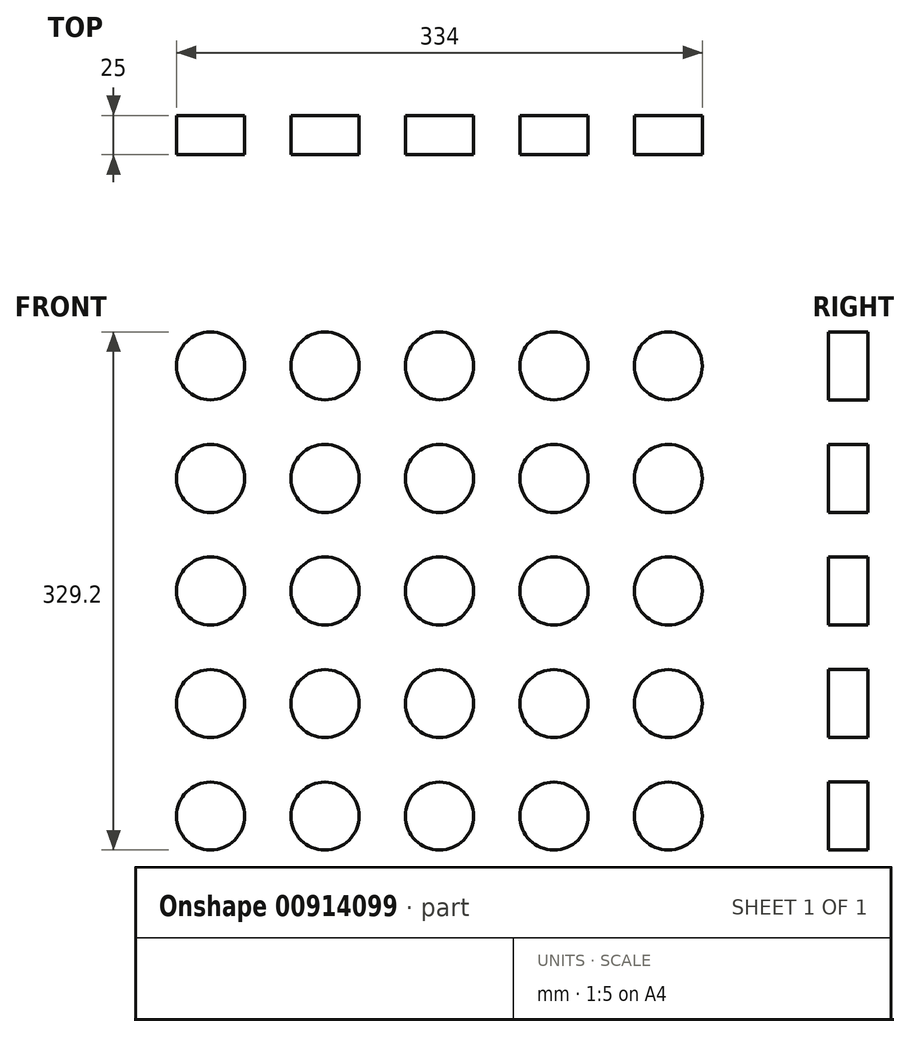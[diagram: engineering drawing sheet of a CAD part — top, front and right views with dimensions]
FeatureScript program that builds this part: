
annotation { "Feature Type Name" : "Feature", "Feature Type Description" : "" }
export const myFeature = defineFeature(function(context is Context, id is Id, definition is map)
    precondition{}
    {
        {
            var Q0;
            Q0=qCreatedBy(makeId("Front.planeOp"),FACE);
            var sketch = newSketch(context, id + "F0", { "sketchPlane" : qUnion([Q0])});
            skCircle(sketch, "E0", {"center": v(0, 0) * mm, "radius": 21.6 * mm});
            skCircle(sketch, "E1.0.1.0", {"center": v(0, 71.5) * mm, "radius": 21.6 * mm});
            skCircle(sketch, "E1.0.2.0", {"center": v(0, 143) * mm, "radius": 21.6 * mm});
            skCircle(sketch, "E1.0.3.0", {"center": v(0, 214.5) * mm, "radius": 21.6 * mm});
            skCircle(sketch, "E1.0.4.0", {"center": v(0, 286) * mm, "radius": 21.6 * mm});
            skCircle(sketch, "E1.1.0.0", {"center": v(72.7, 0) * mm, "radius": 21.6 * mm});
            skCircle(sketch, "E1.1.1.0", {"center": v(72.7, 71.5) * mm, "radius": 21.6 * mm});
            skCircle(sketch, "E1.1.2.0", {"center": v(72.7, 143) * mm, "radius": 21.6 * mm});
            skCircle(sketch, "E1.1.3.0", {"center": v(72.7, 214.5) * mm, "radius": 21.6 * mm});
            skCircle(sketch, "E1.1.4.0", {"center": v(72.7, 286) * mm, "radius": 21.6 * mm});
            skCircle(sketch, "E1.2.0.0", {"center": v(145.4, 0) * mm, "radius": 21.6 * mm});
            skCircle(sketch, "E1.2.1.0", {"center": v(145.4, 71.5) * mm, "radius": 21.6 * mm});
            skCircle(sketch, "E1.2.2.0", {"center": v(145.4, 143) * mm, "radius": 21.6 * mm});
            skCircle(sketch, "E1.2.3.0", {"center": v(145.4, 214.5) * mm, "radius": 21.6 * mm});
            skCircle(sketch, "E1.2.4.0", {"center": v(145.4, 286) * mm, "radius": 21.6 * mm});
            skCircle(sketch, "E1.3.0.0", {"center": v(218.1, 0) * mm, "radius": 21.6 * mm});
            skCircle(sketch, "E1.3.1.0", {"center": v(218.1, 71.5) * mm, "radius": 21.6 * mm});
            skCircle(sketch, "E1.3.2.0", {"center": v(218.1, 143) * mm, "radius": 21.6 * mm});
            skCircle(sketch, "E1.3.3.0", {"center": v(218.1, 214.5) * mm, "radius": 21.6 * mm});
            skCircle(sketch, "E1.3.4.0", {"center": v(218.1, 286) * mm, "radius": 21.6 * mm});
            skCircle(sketch, "E1.4.0.0", {"center": v(290.8, 0) * mm, "radius": 21.6 * mm});
            skCircle(sketch, "E1.4.1.0", {"center": v(290.8, 71.5) * mm, "radius": 21.6 * mm});
            skCircle(sketch, "E1.4.2.0", {"center": v(290.8, 143) * mm, "radius": 21.6 * mm});
            skCircle(sketch, "E1.4.3.0", {"center": v(290.8, 214.5) * mm, "radius": 21.6 * mm});
            skCircle(sketch, "E1.4.4.0", {"center": v(290.8, 286) * mm, "radius": 21.6 * mm});
            skLineSegment(sketch, "E1.direction1", {"start": v(0, 0) * mm, "end": v(72.7, 0) * mm, "construction": true});
            skLineSegment(sketch, "E1.direction2", {"start": v(0, 0) * mm, "end": v(0, 71.5) * mm, "construction": true});
            skSolve(sketch);
        }
        {
            var Q0;
            Q0 = qConstructionFilter(qBodyType(qCreatedBy(id + "F0" ,EDGE), BodyType.WIRE), ConstructionObject.NO);
            extrude(context, id + "F1", {"bodyType" : ToolBodyType.SURFACE, "surfaceEntities" : qUnion([Q0]), "depth" : 25 * mm, "offsetDistance" : 25 * mm});
        }
    });
